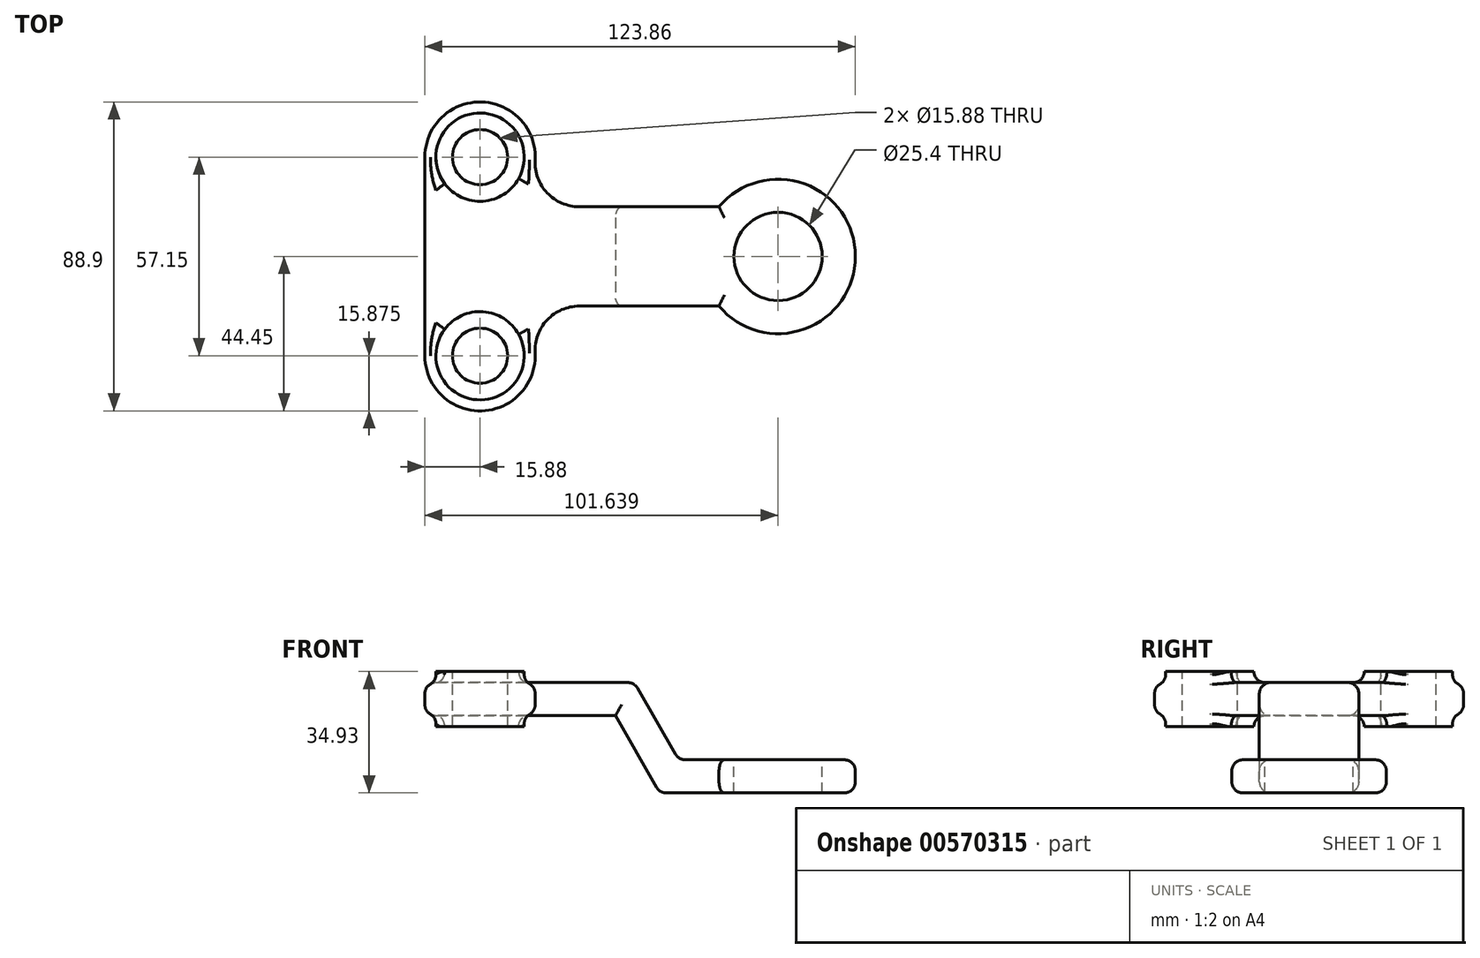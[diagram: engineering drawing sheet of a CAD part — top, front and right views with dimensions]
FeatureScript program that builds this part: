
annotation { "Feature Type Name" : "Feature", "Feature Type Description" : "" }
export const myFeature = defineFeature(function(context is Context, id is Id, definition is map)
    precondition{}
    {
        {
            var Q0;
            Q0=qCreatedBy(makeId("Top.planeOp"),FACE);
            var sketch = newSketch(context, id + "F0", { "sketchPlane" : qUnion([Q0])});
            skLineSegment(sketch, "E0", {"start": v(0, 0) * mm, "end": v(0, 28.58) * mm});
            skLineSegment(sketch, "E1", {"start": v(0, 0) * mm, "end": v(44.45, 0) * mm});
            skArc(sketch, "E2", {"start": v(15.85, 27.7) * mm, "mid": v(0.44, 44.44) * mm, "end": v(-15.87, 28.58) * mm});
            skArc(sketch, "E3.MirrorC", {"start": v(15.85, -27.7) * mm, "mid": v(0.44, -44.44) * mm, "end": v(-15.88, -28.58) * mm});
            skLineSegment(sketch, "E4", {"start": v(44.45, 14.3) * mm, "end": v(44.45, -14.3) * mm});
            skArc(sketch, "E5", {"start": v(15.85, 27.7) * mm, "mid": v(19.3, 18.27) * mm, "end": v(28.53, 14.3) * mm});
            skLineSegment(sketch, "E6.trimOffspring", {"start": v(28.53, 14.3) * mm, "end": v(44.45, 14.3) * mm});
            skPoint(sketch, "E7.0.start.orphan", {"position": v(0, 14.3) * mm});
            skPoint(sketch, "E8.MirrorCS.start.orphan", {"position": v(0, -14.3) * mm});
            skArc(sketch, "E9.MirrorCS", {"start": v(15.85, -27.7) * mm, "mid": v(19.3, -18.27) * mm, "end": v(28.53, -14.3) * mm});
            skLineSegment(sketch, "E10.MirrorCS", {"start": v(28.53, -14.3) * mm, "end": v(44.45, -14.3) * mm});
            skLineSegment(sketch, "E11", {"start": v(-15.88, -28.58) * mm, "end": v(-15.87, 28.58) * mm});
            skCircle(sketch, "E12", {"center": v(0, 28.58) * mm, "radius": 7.94 * mm});
            skCircle(sketch, "E13", {"center": v(0, -28.58) * mm, "radius": 7.94 * mm});
            skCircle(sketch, "E14", {"center": v(0, 28.58) * mm, "radius": 12.7 * mm});
            skCircle(sketch, "E15", {"center": v(0, -28.58) * mm, "radius": 12.7 * mm});
            skSolve(sketch);
        }
        {
            var Q0;
            Q0=makeQuery(id+"F0.imprint","IMPRINT",FACE,{"disambiguationData":[TD([[makeQuery(id+"F0.imprint","IMPRINT",EDGE,{"derivedFrom":sQuery(id+"F0.wireOp",EDGE,"E2")}),1.0]])]});
            var Q1;
            Q1=makeQuery(id+"F0.imprint","IMPRINT",FACE,{"disambiguationData":[TD([[makeQuery(id+"F0.imprint","IMPRINT",EDGE,{"derivedFrom":sQuery(id+"F0.wireOp",EDGE,"E12")}),-1.0]])]});
            var Q2;
            Q2=makeQuery(id+"F0.imprint","IMPRINT",FACE,{"disambiguationData":[TD([[makeQuery(id+"F0.imprint","IMPRINT",EDGE,{"derivedFrom":sQuery(id+"F0.wireOp",EDGE,"E13")}),-1.0]])]});
            extrude(context, id + "F1", {"entities" : qUnion([Q0, Q1, Q2]), "oppositeDirection" : true, "depth" : 9.52 * mm, "offsetDistance" : 25.4 * mm});
        }
        {
            var Q0;
            Q0=makeQuery(id+"F0.imprint","IMPRINT",FACE,{"disambiguationData":[TD([[makeQuery(id+"F0.imprint","IMPRINT",EDGE,{"derivedFrom":sQuery(id+"F0.wireOp",EDGE,"E12")}),-1.0]])]});
            var Q1;
            Q1=makeQuery(id+"F0.imprint","IMPRINT",FACE,{"disambiguationData":[TD([[makeQuery(id+"F0.imprint","IMPRINT",EDGE,{"derivedFrom":sQuery(id+"F0.wireOp",EDGE,"E13")}),-1.0]])]});
            extrude(context, id + "F2", {"entities" : qUnion([Q0, Q1]), "operationType" : NewBodyOperationType.ADD, "depth" : 3.17 * mm, "offsetDistance" : 25.4 * mm, "hasSecondDirection" : true, "secondDirectionOppositeDirection" : true, "secondDirectionDepth" : 12.7 * mm});
        }
        {
            var Q0;
            Q0=qCreatedBy(makeId("Top.planeOp"),FACE);
            cPlane(context, id + "F3", {"entities" : qUnion([Q0]), "cplaneType" : CPlaneType.OFFSET, "offset" : 22.22 * mm, "oppositeDirection" : true, "width" : 152.4 * mm, "height" : 152.4 * mm});
        }
        {
            var Q0;
            Q0=qCreatedBy(id+"F3.planeOp",FACE);
            var sketch = newSketch(context, id + "F4", { "sketchPlane" : qUnion([Q0])});
            skLineSegment(sketch, "E16", {"start": v(44.48, 0) * mm, "end": v(85.76, 0) * mm});
            skArc(sketch, "E17", {"start": v(68.75, -14.3) * mm, "mid": v(107.98, 0) * mm, "end": v(68.75, 14.3) * mm});
            skCircle(sketch, "E18", {"center": v(85.76, 0) * mm, "radius": 12.7 * mm});
            skLineSegment(sketch, "E19.0", {"start": v(57.18, -14.3) * mm, "end": v(68.75, -14.3) * mm});
            skLineSegment(sketch, "E20.MirrorCS", {"start": v(57.18, 14.3) * mm, "end": v(68.75, 14.3) * mm});
            skLineSegment(sketch, "E21", {"start": v(57.18, 14.3) * mm, "end": v(57.18, -14.3) * mm});
            skPoint(sketch, "E22.orphan", {"position": v(44.48, 14.3) * mm});
            skPoint(sketch, "E23.orphan", {"position": v(44.48, -14.3) * mm});
            skPoint(sketch, "E24.orphan", {"position": v(85.76, -14.3) * mm});
            skPoint(sketch, "E25.orphan", {"position": v(85.76, 14.3) * mm});
            skSolve(sketch);
        }
        {
            var Q0;
            Q0=makeQuery(id+"F4.imprint","IMPRINT",FACE,{"disambiguationData":[TD([[makeQuery(id+"F4.imprint","IMPRINT",EDGE,{"derivedFrom":sQuery(id+"F4.wireOp",EDGE,"E17")}),1.0]])]});
            extrude(context, id + "F5", {"entities" : qUnion([Q0]), "oppositeDirection" : true, "depth" : 9.52 * mm, "offsetDistance" : 25.4 * mm});
        }
        {
            var Q0;
            Q0=makeQuery(id+"F1.opExtrude","SWEPT_FACE",FACE,{"disambiguationData":[OSD([sQuery(id+"F0.wireOp",EDGE,"E10.MirrorCS")])]});
            var sketch = newSketch(context, id + "F6", { "sketchPlane" : qUnion([Q0])});
            skLineSegment(sketch, "E26", {"start": v(57.18, -22.23) * mm, "end": v(68.75, -22.23) * mm});
            skLineSegment(sketch, "E27", {"start": v(57.18, -31.75) * mm, "end": v(57.18, -22.23) * mm});
            skLineSegment(sketch, "E28", {"start": v(57.18, -31.75) * mm, "end": v(68.75, -31.75) * mm});
            skLineSegment(sketch, "E29", {"start": v(68.75, -31.75) * mm, "end": v(68.75, -22.23) * mm});
            skLineSegment(sketch, "E30", {"start": v(44.45, 0) * mm, "end": v(57.18, -22.23) * mm});
            skLineSegment(sketch, "E31.0", {"start": v(36.19, -4.74) * mm, "end": v(51.66, -31.75) * mm});
            skLineSegment(sketch, "E32", {"start": v(57.18, -31.75) * mm, "end": v(51.66, -31.75) * mm});
            skLineSegment(sketch, "E33", {"start": v(36.19, -4.74) * mm, "end": v(44.45, 0) * mm});
            skPoint(sketch, "E34.end.orphan", {"position": v(0, -20.75) * mm});
            skSolve(sketch);
        }
        {
            var Q0;
            Q0=makeQuery(id+"F6.imprint","IMPRINT",FACE,{"disambiguationData":[TD([[makeQuery(id+"F6.imprint","IMPRINT",EDGE,{"derivedFrom":sQuery(id+"F6.wireOp",EDGE,"E27")}),1.0]])]});
            extrude(context, id + "F7", {"entities" : qUnion([Q0]), "oppositeDirection" : true, "depth" : 28.6 * mm, "offsetDistance" : 25.4 * mm});
        }
        {
            var Q0;
            Q0=makeQuery(id+"F1.opExtrude","SWEPT_BODY",BODY,{"disambiguationData":[OSD([sQuery(id+"F0.wireOp",EDGE,"E2"),sQuery(id+"F0.wireOp",EDGE,"E3.MirrorC"),sQuery(id+"F0.wireOp",EDGE,"E4"),sQuery(id+"F0.wireOp",EDGE,"E5"),sQuery(id+"F0.wireOp",EDGE,"E6.trimOffspring"),sQuery(id+"F0.wireOp",EDGE,"E9.MirrorCS"),sQuery(id+"F0.wireOp",EDGE,"E10.MirrorCS"),sQuery(id+"F0.wireOp",EDGE,"E11"),sQuery(id+"F0.wireOp",EDGE,"E12"),sQuery(id+"F0.wireOp",EDGE,"E13")])]});
            var Q1;
            Q1=makeQuery(id+"F7.opExtrude","SWEPT_BODY",BODY,{"disambiguationData":[OSD([sQuery(id+"F0.wireOp",EDGE,"E4"),sQuery(id+"F0.wireOp",EDGE,"E10.MirrorCS"),sQuery(id+"F6.wireOp",EDGE,"E27"),sQuery(id+"F6.wireOp",EDGE,"E30"),sQuery(id+"F6.wireOp",EDGE,"E31.0"),sQuery(id+"F6.wireOp",EDGE,"E32")])]});
            var Q2;
            Q2=makeQuery(id+"F5.opExtrude","SWEPT_BODY",BODY,{"disambiguationData":[OSD([sQuery(id+"F4.wireOp",EDGE,"E17"),sQuery(id+"F4.wireOp",EDGE,"E18"),sQuery(id+"F4.wireOp",EDGE,"E19.0"),sQuery(id+"F4.wireOp",EDGE,"E20.MirrorCS"),sQuery(id+"F4.wireOp",EDGE,"E21")])]});
            booleanBodies(context, id + "F8", {"operationType" : BooleanOperationType.UNION, "tools" : qUnion([Q0, Q1, Q2])});
        }
        {
            var Q0;
            Q0=makeQuery(id+"F1.opExtrude","CAP_EDGE",EDGE,{"disambiguationData":[OSD([sQuery(id+"F0.wireOp",EDGE,"E11")])],"isStart":true});
            var Q1;
            Q1=makeQuery(id+"F5.opExtrude","CAP_EDGE",EDGE,{"disambiguationData":[OSD([sQuery(id+"F4.wireOp",EDGE,"E17")])],"isStart":true});
            var Q2;
            Q2=makeQuery(id+"F5.opExtrude","CAP_EDGE",EDGE,{"disambiguationData":[OSD([sQuery(id+"F4.wireOp",EDGE,"E19.0")])],"isStart":true});
            var Q3;
            Q3=makeQuery(id+"F5.opExtrude","CAP_EDGE",EDGE,{"disambiguationData":[OSD([sQuery(id+"F4.wireOp",EDGE,"E20.MirrorCS")])],"isStart":true});
            var Q4;
            Q4=makeQuery(id+"F7.opExtrude","CAP_EDGE",EDGE,{"disambiguationData":[OSD([sQuery(id+"F6.wireOp",EDGE,"E30")])],"isStart":true});
            var Q5;
            Q5=makeQuery(id+"F7.opExtrude","CAP_EDGE",EDGE,{"disambiguationData":[OSD([sQuery(id+"F6.wireOp",EDGE,"E30")])],"isStart":false});
            var Q6;
            Q6=makeQuery(id+"F8.opBoolean","MERGE",EDGE,{"derivedFrom":[makeQuery(id+"F5.opExtrude","CAP_EDGE",EDGE,{"disambiguationData":[OSD([sQuery(id+"F4.wireOp",EDGE,"E21")])],"isStart":true}),makeQuery(id+"F7.opExtrude","SWEPT_EDGE",EDGE,{"disambiguationData":[OSD([sQuery(id+"F6.wireOp",EDGE,"E26"),sQuery(id+"F6.wireOp",EDGE,"E27"),sQuery(id+"F6.wireOp",EDGE,"E30")])]})]});
            var Q7;
            {var subQ0=sQuery(id+"F0.wireOp",EDGE,"E4");Q7=makeQuery(id+"F8.opBoolean","MERGE",EDGE,{"derivedFrom":[makeQuery(id+"F1.opExtrude","CAP_EDGE",EDGE,{"disambiguationData":[OSD([subQ0])],"isStart":true}),makeQuery(id+"F7.opExtrude","SWEPT_EDGE",EDGE,{"disambiguationData":[OSD([subQ0,sQuery(id+"F0.wireOp",EDGE,"E10.MirrorCS"),sQuery(id+"F6.wireOp",EDGE,"E30"),sQuery(id+"F6.wireOp",EDGE,"E33")])]})]});}
            fillet(context, id + "F9", {"entities" : qUnion([Q0, Q1, Q2, Q3, Q4, Q5, Q6, Q7]), "radius" : 3.17 * mm, "tangentPropagation" : true, "allowEdgeOverflow" : false});
        }
        {
            var Q0;
            Q0=makeQuery(id+"F1.opExtrude","CAP_EDGE",EDGE,{"disambiguationData":[OSD([sQuery(id+"F0.wireOp",EDGE,"E2")])],"isStart":false});
            var Q1;
            Q1=makeQuery(id+"F5.opExtrude","CAP_EDGE",EDGE,{"disambiguationData":[OSD([sQuery(id+"F4.wireOp",EDGE,"E17")])],"isStart":false});
            var Q2;
            Q2=makeQuery(id+"F8.opBoolean","MERGE",EDGE,{"derivedFrom":[makeQuery(id+"F5.opExtrude","CAP_EDGE",EDGE,{"disambiguationData":[OSD([sQuery(id+"F4.wireOp",EDGE,"E20.MirrorCS")])],"isStart":false}),makeQuery(id+"F7.opExtrude","CAP_EDGE",EDGE,{"disambiguationData":[OSD([sQuery(id+"F6.wireOp",EDGE,"E32")])],"isStart":false})]});
            var Q3;
            Q3=makeQuery(id+"F8.opBoolean","MERGE",EDGE,{"derivedFrom":[makeQuery(id+"F5.opExtrude","CAP_EDGE",EDGE,{"disambiguationData":[OSD([sQuery(id+"F4.wireOp",EDGE,"E19.0")])],"isStart":false}),makeQuery(id+"F7.opExtrude","CAP_EDGE",EDGE,{"disambiguationData":[OSD([sQuery(id+"F6.wireOp",EDGE,"E32")])],"isStart":true})]});
            var Q4;
            Q4=makeQuery(id+"F7.opExtrude","CAP_EDGE",EDGE,{"disambiguationData":[OSD([sQuery(id+"F6.wireOp",EDGE,"E31.0")])],"isStart":true});
            var Q5;
            Q5=makeQuery(id+"F7.opExtrude","CAP_EDGE",EDGE,{"disambiguationData":[OSD([sQuery(id+"F6.wireOp",EDGE,"E31.0")])],"isStart":false});
            var Q6;
            Q6=makeQuery(id+"F7.opExtrude","SWEPT_EDGE",EDGE,{"disambiguationData":[OSD([sQuery(id+"F6.wireOp",EDGE,"E31.0"),sQuery(id+"F6.wireOp",EDGE,"E32")])]});
            var Q7;
            Q7=makeQuery(id+"F7.opExtrude","SWEPT_EDGE",EDGE,{"disambiguationData":[OSD([sQuery(id+"F0.wireOp",EDGE,"E10.MirrorCS"),sQuery(id+"F6.wireOp",EDGE,"E31.0")])]});
            fillet(context, id + "F10", {"entities" : qUnion([Q0, Q1, Q2, Q3, Q4, Q5, Q6, Q7]), "radius" : 3.17 * mm, "tangentPropagation" : true, "allowEdgeOverflow" : false});
        }
        {
            var Q0;
            Q0=makeQuery(id+"F2.boolean.opBoolean","INTERSECT",EDGE,{"derivedFrom":[makeQuery(id+"F1.opExtrude","CAP_FACE",FACE,{"disambiguationData":[OSD([sQuery(id+"F0.wireOp",EDGE,"E2"),sQuery(id+"F0.wireOp",EDGE,"E3.MirrorC"),sQuery(id+"F0.wireOp",EDGE,"E4"),sQuery(id+"F0.wireOp",EDGE,"E5"),sQuery(id+"F0.wireOp",EDGE,"E6.trimOffspring"),sQuery(id+"F0.wireOp",EDGE,"E9.MirrorCS"),sQuery(id+"F0.wireOp",EDGE,"E10.MirrorCS"),sQuery(id+"F0.wireOp",EDGE,"E11"),sQuery(id+"F0.wireOp",EDGE,"E12"),sQuery(id+"F0.wireOp",EDGE,"E13")])],"isStart":false}),makeQuery(id+"F2.opExtrude","SWEPT_FACE",FACE,{"disambiguationData":[OSD([sQuery(id+"F0.wireOp",EDGE,"E15")])]})]});
            var Q1;
            Q1=makeQuery(id+"F2.boolean.opBoolean","INTERSECT",EDGE,{"derivedFrom":[makeQuery(id+"F1.opExtrude","CAP_FACE",FACE,{"disambiguationData":[OSD([sQuery(id+"F0.wireOp",EDGE,"E2"),sQuery(id+"F0.wireOp",EDGE,"E3.MirrorC"),sQuery(id+"F0.wireOp",EDGE,"E4"),sQuery(id+"F0.wireOp",EDGE,"E5"),sQuery(id+"F0.wireOp",EDGE,"E6.trimOffspring"),sQuery(id+"F0.wireOp",EDGE,"E9.MirrorCS"),sQuery(id+"F0.wireOp",EDGE,"E10.MirrorCS"),sQuery(id+"F0.wireOp",EDGE,"E11"),sQuery(id+"F0.wireOp",EDGE,"E12"),sQuery(id+"F0.wireOp",EDGE,"E13")])],"isStart":false}),makeQuery(id+"F2.opExtrude","SWEPT_FACE",FACE,{"disambiguationData":[OSD([sQuery(id+"F0.wireOp",EDGE,"E14")])]})]});
            fillet(context, id + "F11", {"entities" : qUnion([Q0, Q1]), "radius" : 3.17 * mm, "tangentPropagation" : true, "allowEdgeOverflow" : false});
        }
        {
            var Q0;
            Q0=makeQuery(id+"F2.boolean.opBoolean","INTERSECT",EDGE,{"derivedFrom":[makeQuery(id+"F1.opExtrude","CAP_FACE",FACE,{"disambiguationData":[OSD([sQuery(id+"F0.wireOp",EDGE,"E2"),sQuery(id+"F0.wireOp",EDGE,"E3.MirrorC"),sQuery(id+"F0.wireOp",EDGE,"E4"),sQuery(id+"F0.wireOp",EDGE,"E5"),sQuery(id+"F0.wireOp",EDGE,"E6.trimOffspring"),sQuery(id+"F0.wireOp",EDGE,"E9.MirrorCS"),sQuery(id+"F0.wireOp",EDGE,"E10.MirrorCS"),sQuery(id+"F0.wireOp",EDGE,"E11"),sQuery(id+"F0.wireOp",EDGE,"E12"),sQuery(id+"F0.wireOp",EDGE,"E13")])],"isStart":true}),makeQuery(id+"F2.opExtrude","SWEPT_FACE",FACE,{"disambiguationData":[OSD([sQuery(id+"F0.wireOp",EDGE,"E15")])]})]});
            var Q1;
            Q1=makeQuery(id+"F2.boolean.opBoolean","INTERSECT",EDGE,{"derivedFrom":[makeQuery(id+"F1.opExtrude","CAP_FACE",FACE,{"disambiguationData":[OSD([sQuery(id+"F0.wireOp",EDGE,"E2"),sQuery(id+"F0.wireOp",EDGE,"E3.MirrorC"),sQuery(id+"F0.wireOp",EDGE,"E4"),sQuery(id+"F0.wireOp",EDGE,"E5"),sQuery(id+"F0.wireOp",EDGE,"E6.trimOffspring"),sQuery(id+"F0.wireOp",EDGE,"E9.MirrorCS"),sQuery(id+"F0.wireOp",EDGE,"E10.MirrorCS"),sQuery(id+"F0.wireOp",EDGE,"E11"),sQuery(id+"F0.wireOp",EDGE,"E12"),sQuery(id+"F0.wireOp",EDGE,"E13")])],"isStart":true}),makeQuery(id+"F2.opExtrude","SWEPT_FACE",FACE,{"disambiguationData":[OSD([sQuery(id+"F0.wireOp",EDGE,"E14")])]})]});
            fillet(context, id + "F12", {"entities" : qUnion([Q0, Q1]), "radius" : 3.17 * mm, "tangentPropagation" : true, "allowEdgeOverflow" : false});
        }
    });
